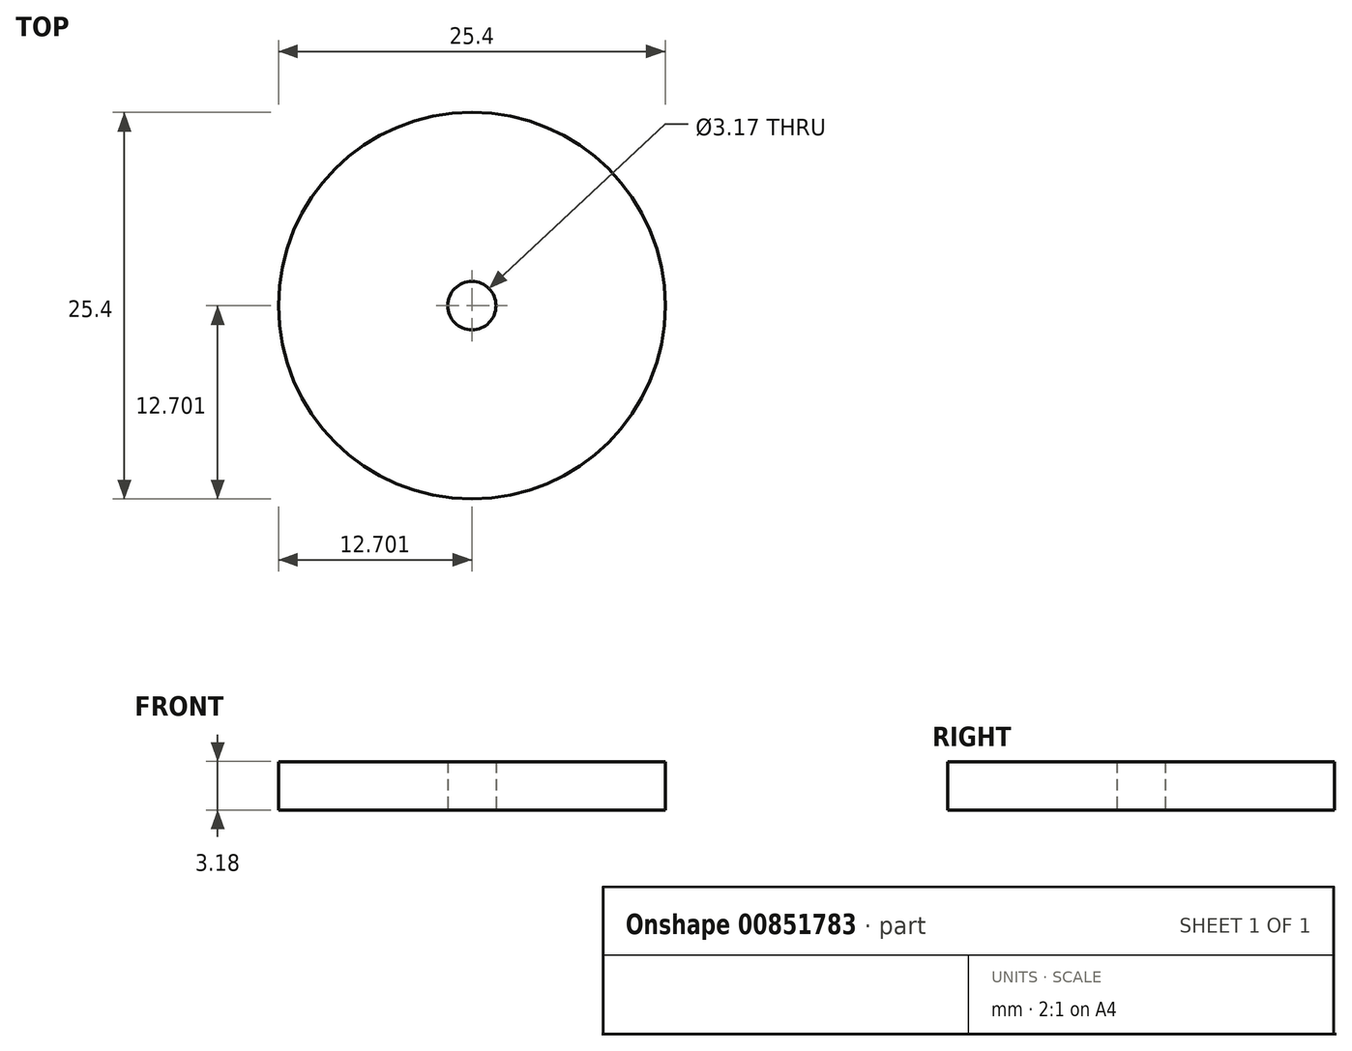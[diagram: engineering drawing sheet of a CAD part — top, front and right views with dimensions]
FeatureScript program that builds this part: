
annotation { "Feature Type Name" : "Feature", "Feature Type Description" : "" }
export const myFeature = defineFeature(function(context is Context, id is Id, definition is map)
    precondition{}
    {
        {
            var Q0;
            Q0=qCreatedBy(makeId("Top.planeOp"),FACE);
            var sketch = newSketch(context, id + "F0", { "sketchPlane" : qUnion([Q0])});
            skCircle(sketch, "E0", {"center": v(-64.72, 26.47) * mm, "radius": 12.7 * mm});
            skCircle(sketch, "E1", {"center": v(-64.72, 26.47) * mm, "radius": 1.59 * mm});
            skSolve(sketch);
        }
        {
            var Q0;
            Q0=makeQuery(id+"F0.imprint","IMPRINT",FACE,{"disambiguationData":[TD([[makeQuery(id+"F0.imprint","IMPRINT",EDGE,{"derivedFrom":sQuery(id+"F0.wireOp",EDGE,"E0")}),1.0]])]});
            extrude(context, id + "F1", {"entities" : qUnion([Q0]), "depth" : 3.17 * mm, "offsetDistance" : 25.4 * mm});
        }
    });
